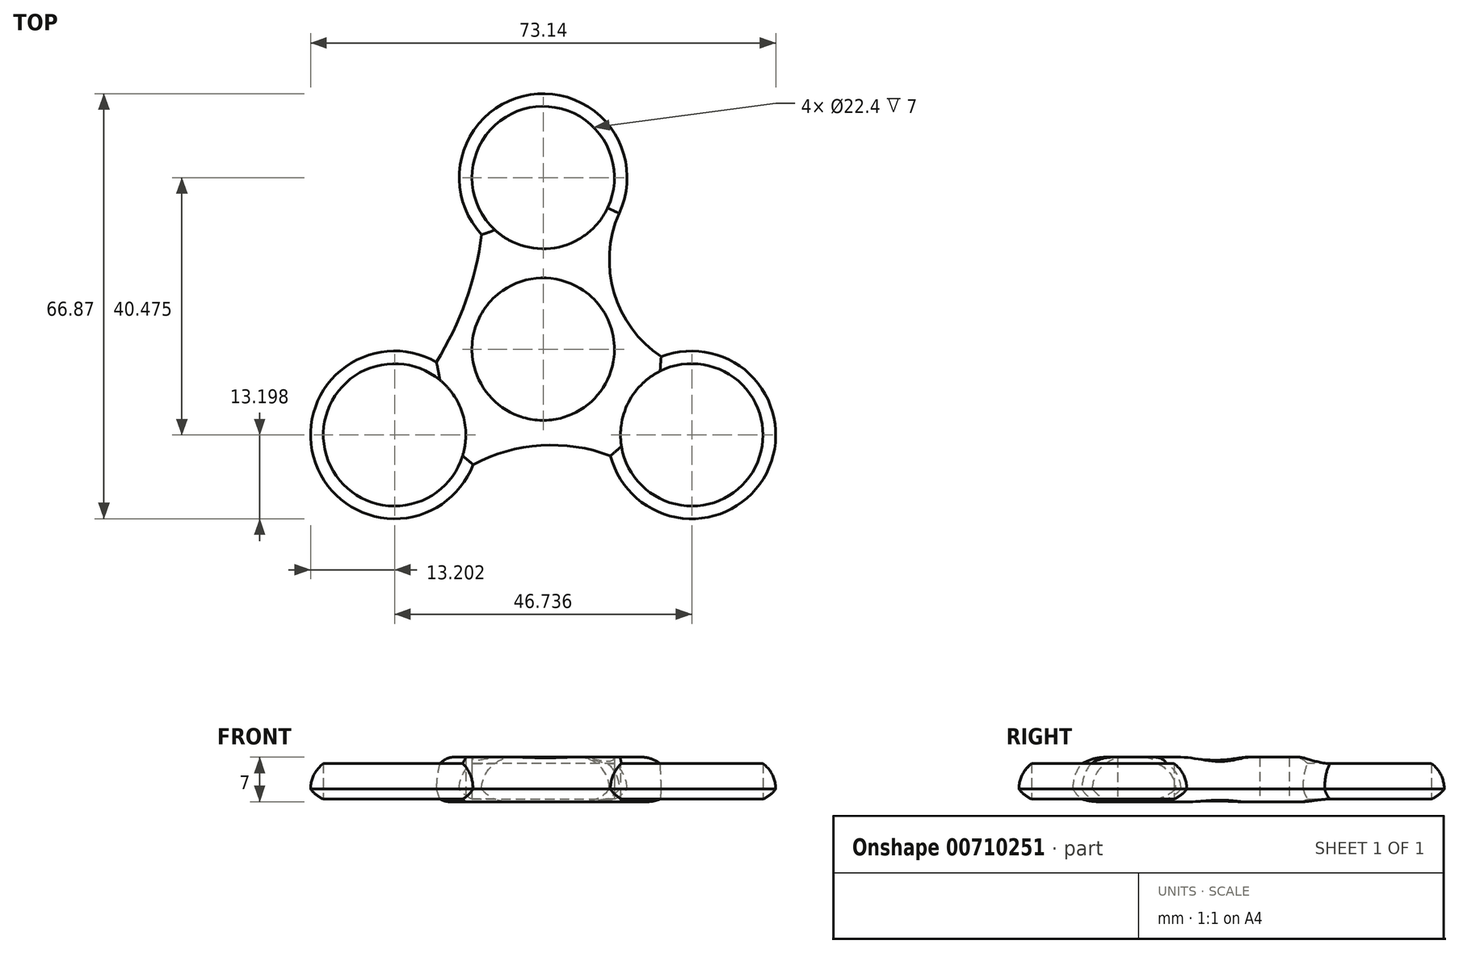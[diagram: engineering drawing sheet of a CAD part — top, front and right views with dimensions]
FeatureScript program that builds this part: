
annotation { "Feature Type Name" : "Feature", "Feature Type Description" : "" }
export const myFeature = defineFeature(function(context is Context, id is Id, definition is map)
    precondition{}
    {
        {
            var Q0;
            Q0=qCreatedBy(makeId("Top.planeOp"),FACE);
            var sketch = newSketch(context, id + "F0", { "sketchPlane" : qUnion([Q0])});
            skCircle(sketch, "E0", {"center": v(0, 0) * mm, "radius": 11.2 * mm});
            skCircle(sketch, "E1", {"center": v(0, 0) * mm, "radius": 13.2 * mm});
            skCircle(sketch, "E2", {"center": v(0, 26.98) * mm, "radius": 11.2 * mm});
            skArc(sketch, "E3", {"start": v(11.95, 21.37) * mm, "mid": v(-2.03, 40.03) * mm, "end": v(-9.68, 18) * mm});
            skArc(sketch, "E4.1.0", {"start": v(-16.8, -2.04) * mm, "mid": v(-35.8, -17.94) * mm, "end": v(-11.03, -18.17) * mm});
            skCircle(sketch, "E4.1.1", {"center": v(-23.37, -13.5) * mm, "radius": 11.2 * mm});
            skArc(sketch, "E4.2.0", {"start": v(10.59, -16.79) * mm, "mid": v(35.12, -19.5) * mm, "end": v(18.56, -1.2) * mm});
            skCircle(sketch, "E4.2.1", {"center": v(23.37, -13.5) * mm, "radius": 11.2 * mm});
            skArc(sketch, "E5", {"start": v(-16.8, -2.04) * mm, "mid": v(-12.16, 7.6) * mm, "end": v(-9.68, 18) * mm});
            skArc(sketch, "E6", {"start": v(10.59, -16.79) * mm, "mid": v(-0.37, -15.15) * mm, "end": v(-11.03, -18.17) * mm});
            skArc(sketch, "E7", {"start": v(12.1, 21.72) * mm, "mid": v(11.09, 9.07) * mm, "end": v(18.56, -1.2) * mm});
            skSolve(sketch);
        }
        {
            var Q0;
            Q0 = qSketchRegion(id + "F0", true);
            var Q1;
            Q1=makeQuery(id+"F0.imprint","IMPRINT",FACE,{"disambiguationData":[TD([[makeQuery(id+"F0.imprint","IMPRINT",EDGE,{"derivedFrom":sQuery(id+"F0.wireOp",EDGE,"E0")}),-1.0]])]});
            extrude(context, id + "F1", {"entities" : qUnion([Q0, Q1]), "depth" : 7 * mm, "offsetDistance" : 25 * mm});
        }
        {
            var Q0;
            Q0=makeQuery(id+"F1.opExtrude","CAP_EDGE",EDGE,{"disambiguationData":[OSD([sQuery(id+"F0.wireOp",EDGE,"E7")])],"isStart":false});
            var Q1;
            Q1=makeQuery(id+"F1.opExtrude","CAP_EDGE",EDGE,{"disambiguationData":[OSD([sQuery(id+"F0.wireOp",EDGE,"E5")])],"isStart":false});
            var Q2;
            Q2=makeQuery(id+"F1.opExtrude","CAP_EDGE",EDGE,{"disambiguationData":[OSD([sQuery(id+"F0.wireOp",EDGE,"E6")])],"isStart":false});
            var Q3;
            Q3=makeQuery(id+"F1.opExtrude","CAP_EDGE",EDGE,{"disambiguationData":[OSD([sQuery(id+"F0.wireOp",EDGE,"E4.1.0")])],"isStart":false});
            var Q4;
            Q4=makeQuery(id+"F1.opExtrude","CAP_EDGE",EDGE,{"disambiguationData":[OSD([sQuery(id+"F0.wireOp",EDGE,"E4.2.0")])],"isStart":false});
            var Q5;
            Q5=makeQuery(id+"F1.opExtrude","CAP_EDGE",EDGE,{"disambiguationData":[OSD([sQuery(id+"F0.wireOp",EDGE,"E3")])],"isStart":false});
            fillet(context, id + "F2", {"entities" : qUnion([Q0, Q1, Q2, Q3, Q4, Q5]), "radius" : 5 * mm, "tangentPropagation" : true, "allowEdgeOverflow" : false});
        }
        {
            var Q0;
            Q0=makeQuery(id+"F1.opExtrude","CAP_EDGE",EDGE,{"disambiguationData":[OSD([sQuery(id+"F0.wireOp",EDGE,"E7")])],"isStart":true});
            var Q1;
            Q1=makeQuery(id+"F1.opExtrude","CAP_EDGE",EDGE,{"disambiguationData":[OSD([sQuery(id+"F0.wireOp",EDGE,"E5")])],"isStart":true});
            var Q2;
            Q2=makeQuery(id+"F1.opExtrude","CAP_EDGE",EDGE,{"disambiguationData":[OSD([sQuery(id+"F0.wireOp",EDGE,"E6")])],"isStart":true});
            fillet(context, id + "F3", {"entities" : qUnion([Q0, Q1, Q2]), "radius" : 5 * mm, "tangentPropagation" : true, "allowEdgeOverflow" : false});
        }
        {
            var Q0;
            Q0=makeQuery(id+"F1.opExtrude","CAP_EDGE",EDGE,{"disambiguationData":[OSD([sQuery(id+"F0.wireOp",EDGE,"E3")])],"isStart":true});
            var Q1;
            Q1=makeQuery(id+"F1.opExtrude","CAP_EDGE",EDGE,{"disambiguationData":[OSD([sQuery(id+"F0.wireOp",EDGE,"E4.1.0")])],"isStart":true});
            var Q2;
            Q2=makeQuery(id+"F1.opExtrude","CAP_EDGE",EDGE,{"disambiguationData":[OSD([sQuery(id+"F0.wireOp",EDGE,"E4.2.0")])],"isStart":true});
            fillet(context, id + "F4", {"entities" : qUnion([Q0, Q1, Q2]), "radius" : 5 * mm, "tangentPropagation" : true, "allowEdgeOverflow" : false});
        }
    });
